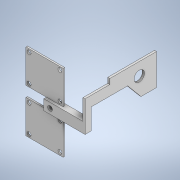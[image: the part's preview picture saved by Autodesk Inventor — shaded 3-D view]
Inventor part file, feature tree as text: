
AUTODESK INVENTOR PART (.ipt)
format: ipt  version: 2020.2 (Build 242310000, 310)  size: 330,240 bytes
history: native  units: mm
features: sketch x15, extrude x12, hole x4, projected_geometry x2
ambient origin geometry x8: Origin, YZ Plane, XZ Plane, XY Plane, X Axis, Y Axis, Z Axis, Center Point
bodies: Body1 (feature_tree), Body2 (feature_tree)
feature tree (33):
  extrude  "Extrusion7"  Depth=6.08mm
  hole  "Hole4"  [1 undecoded]
  sketch  "Sketch16"  dims[d70=12.16mm d71=10.0mm]
  extrude  "Extrusion8"  Depth=10.0mm
  hole  "Hole5"  [1 undecoded]
  extrude  "Extrusion9"  Depth=32.05mm
  extrude  "Extrusion10"  Depth=32.05mm
  extrude  "Extrusion11"  Depth=3.0mm
  hole  "Hole6"  [1 undecoded]
  hole  "Hole7"  [1 undecoded]
  extrude  "Extrusion13"  Depth=26.05mm
  extrude  "Extrusion14"  Depth=4.0mm TaperAngle=0.0deg
  extrude  "Extrusion15"  Depth=10.0mm
  extrude  "Extrusion17"  TaperAngle=90.0deg  [1 undecoded]
  extrude  "Extrusion18"  Depth=45.0mm
  extrude  "Extrusion19"  TaperAngle=90.0deg  [1 undecoded]
  extrude  "Extrusion20"  Depth=25.0mm
  sketch  "Sketch14"  dims[d66=6.08mm d67=6.08mm]
  sketch  "Sketch15"  dims[d68=5.0mm d69=90.0deg]
  sketch  "Sketch17"  dims[d72=2.0mm d73=0.0mm]
  projected_geometry  "Projected Loop2"
  sketch  "Sketch18"  dims[d74=4.5mm d75=6.0mm d76=9.4mm d77=2.0mm d78=90.0deg d79=8.0mm d80=20.594885mm d81=10.0mm]
  projected_geometry  "Projected Loop3"
  sketch  "Sketch19"  dims[d82=35.7mm d83=32.05mm]
  sketch  "Sketch21"  dims[d84=35.7mm d85=32.05mm]
  sketch  "Sketch22"  dims[d86=3.0mm d87=3.0mm]
  sketch  "Sketch23"  dims[d88=29.7mm d89=26.05mm]
  sketch  "Sketch24"  dims[d90=3.0mm d91=3.0mm]
  sketch  "Sketch25"  dims[d92=29.7mm d93=26.05mm]
  sketch  "Sketch27"  dims[d94=1.5mm d95=0.0mm]
  sketch  "Sketch28"  dims[d96=3.9mm d97=6.0mm d98=8.2mm d99=2.0mm d100=90.0deg d101=8.0mm d102=20.594885mm d103=4.0mm d104=0.0mm]
  sketch  "Sketch29"  dims[d105=35.0mm d106=0.0mm d107=10.0mm]
  sketch  "Sketch30"  dims[d108=50.0mm d109=90.0deg d110=45.0mm d111=90.0deg d112=25.0mm d113=2.5mm d114=0.0mm d118=14.05mm d119=90.0deg d120=6.713mm d121=90.0deg d122=10.0mm d123=6.0mm d124=8.2mm d125=2.0mm d126=90.0deg d127=8.0mm d128=20.594885mm d129=8.0mm d130=90.0deg d131=17.5mm d132=90.0deg d133=35.0mm d134=4.2mm d135=6.0mm d136=8.2mm d137=2.0mm d138=90.0deg d139=8.0mm d140=20.594885mm d141=9.0mm d142=90.0deg d145=35.0mm d146=0.0mm d147=11.0mm d148=135.0deg d149=20.0mm d150=35.0mm d151=0.0mm d152=20.0mm d153=90.0deg d154=90.0deg d155=11.45mm d156=4.669mm d157=90.0deg d158=8.0mm d159=17.5mm d160=35.0mm d161=4.2mm d162=4.2mm d163=10.0mm d164=2.0mm d165=0.0mm d166=2.0mm d167=0.0mm d168=35.0mm d169=2.0mm d170=10.0mm d171=0.0mm d172=10.0mm d175=10.0mm d176=0.0mm d177=1.0mm d178=5.0mm d179=0.0mm d180=10.0mm d181=35.0mm d182=0.0mm d183=20.0mm d184=22.68928mm d185=15.0mm d186=30.0mm d187=45.0mm d188=180.0deg d189=5.0mm d190=90.0deg d191=2.0mm d192=0.0mm d193=16.692mm d194=12.189mm d195=10.0mm d196=10.0mm d197=0.0mm]
note: 6 required parameter values undecoded (feature->parameter linkage not recoverable at this tier; creation-order binding heuristic only, values carry confidence <= 0.55)
